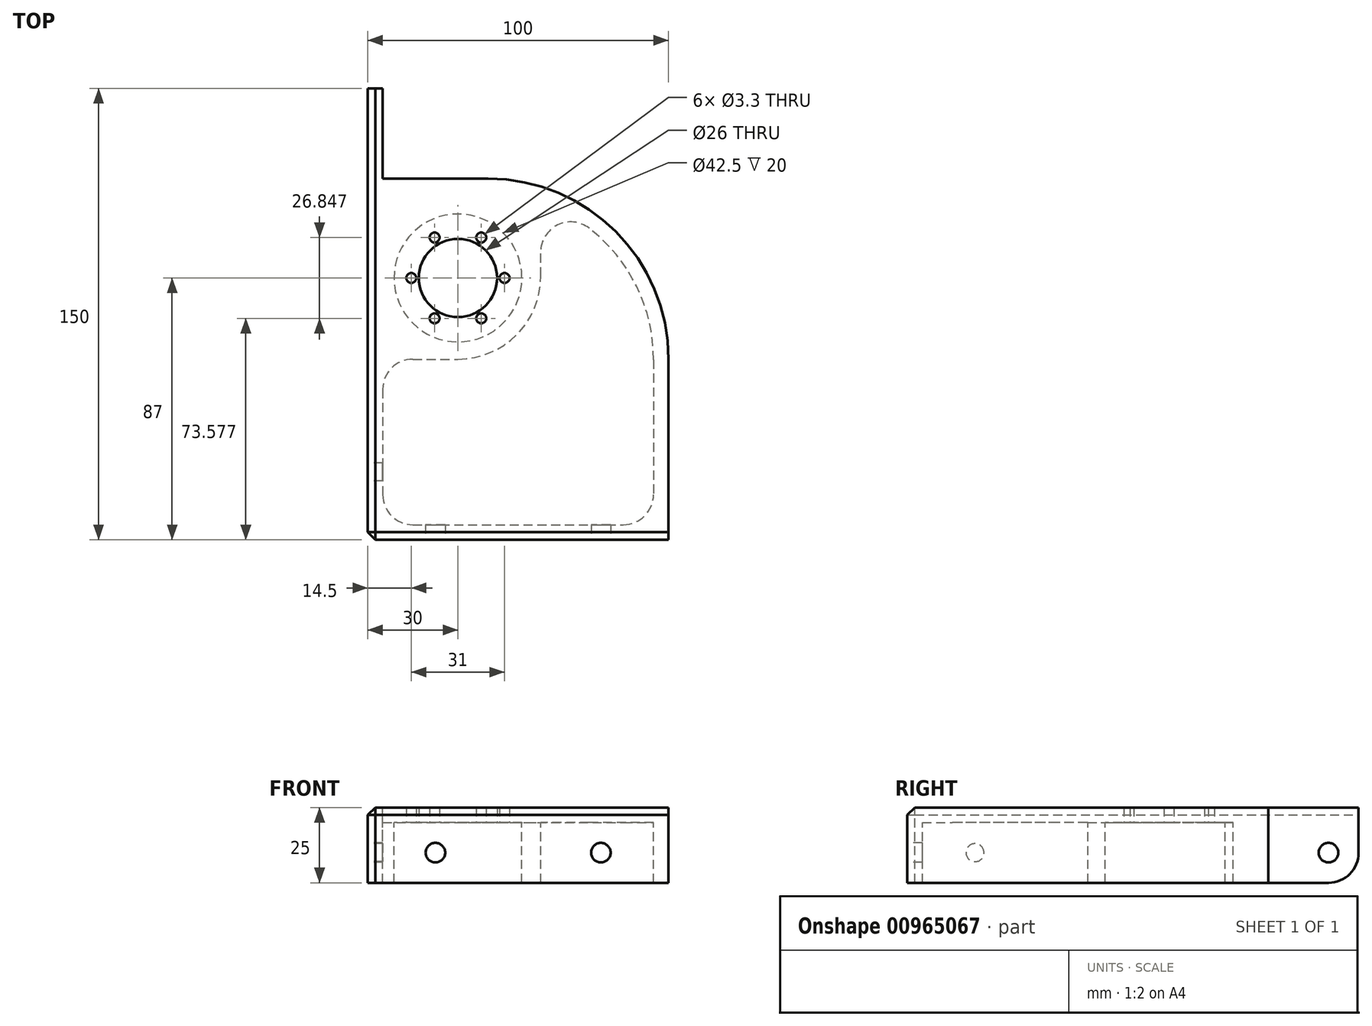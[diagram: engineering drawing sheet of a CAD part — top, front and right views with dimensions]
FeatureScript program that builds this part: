
annotation { "Feature Type Name" : "Feature", "Feature Type Description" : "" }
export const myFeature = defineFeature(function(context is Context, id is Id, definition is map)
    precondition{}
    {
        {
            var Q0;
            Q0=qCreatedBy(makeId("Top.planeOp"),FACE);
            var sketch = newSketch(context, id + "F0", { "sketchPlane" : qUnion([Q0])});
            skLineSegment(sketch, "E0", {"start": v(0, 0) * mm, "end": v(0, 120) * mm});
            skLineSegment(sketch, "E1", {"start": v(100, 0) * mm, "end": v(0, 0) * mm});
            skLineSegment(sketch, "E2", {"start": v(0, 120) * mm, "end": v(5, 120) * mm});
            skLineSegment(sketch, "E3", {"start": v(100, 5) * mm, "end": v(100, 0) * mm});
            skLineSegment(sketch, "E4", {"start": v(5, 120) * mm, "end": v(5, 5) * mm});
            skLineSegment(sketch, "E5", {"start": v(5, 5) * mm, "end": v(100, 5) * mm});
            skCircle(sketch, "E6", {"center": v(30, 87) * mm, "radius": 13 * mm});
            skLineSegment(sketch, "E7", {"start": v(5, 120) * mm, "end": v(40, 120) * mm});
            skLineSegment(sketch, "E8", {"start": v(100, 60) * mm, "end": v(100, 5) * mm});
            skLineSegment(sketch, "E9", {"start": v(44.72, 87) * mm, "end": v(14.37, 87) * mm, "construction": true});
            skLineSegment(sketch, "E10", {"start": v(30, 105.06) * mm, "end": v(30, 59.63) * mm, "construction": true});
            skLineSegment(sketch, "E11", {"start": v(19.21, 97.79) * mm, "end": v(41.7, 75.3) * mm, "construction": true});
            skLineSegment(sketch, "E12", {"start": v(40.55, 97.55) * mm, "end": v(19.07, 76.07) * mm, "construction": true});
            skCircle(sketch, "E13", {"center": v(22.25, 73.58) * mm, "radius": 1.65 * mm});
            skCircle(sketch, "E14.1.0", {"center": v(37.75, 73.58) * mm, "radius": 1.65 * mm});
            skCircle(sketch, "E14.2.0", {"center": v(45.5, 87) * mm, "radius": 1.65 * mm});
            skCircle(sketch, "E14.3.0", {"center": v(37.75, 100.42) * mm, "radius": 1.65 * mm});
            skCircle(sketch, "E14.4.0", {"center": v(22.25, 100.42) * mm, "radius": 1.65 * mm});
            skCircle(sketch, "E14.5.0", {"center": v(14.5, 87) * mm, "radius": 1.65 * mm});
            skPoint(sketch, "E15.visualSharp", {"position": v(100, 120) * mm});
            skArc(sketch, "E15.filletArc", {"start": v(100, 60) * mm, "mid": v(82.43, 102.43) * mm, "end": v(40, 120) * mm});
            skLineSegment(sketch, "E16", {"start": v(-20, -20) * mm, "end": v(-20, 140) * mm, "construction": true});
            skLineSegment(sketch, "E17", {"start": v(-20, 140) * mm, "end": v(0, 140) * mm, "construction": true});
            skLineSegment(sketch, "E18", {"start": v(-10, -167) * mm, "end": v(-10, 160.54) * mm, "construction": true});
            skLineSegment(sketch, "E19", {"start": v(-27.5, -172.08) * mm, "end": v(-27.5, -121.08) * mm, "construction": true});
            skLineSegment(sketch, "E20", {"start": v(-27.5, -121.08) * mm, "end": v(37.5, -121.08) * mm, "construction": true});
            skLineSegment(sketch, "E21", {"start": v(37.5, -121.08) * mm, "end": v(37.5, -127.08) * mm, "construction": true});
            skLineSegment(sketch, "E22", {"start": v(37.5, -127.08) * mm, "end": v(7.5, -127.08) * mm, "construction": true});
            skLineSegment(sketch, "E23", {"start": v(7.5, -127.08) * mm, "end": v(7.5, -172.08) * mm, "construction": true});
            skLineSegment(sketch, "E24", {"start": v(7.5, -172.08) * mm, "end": v(2.5, -172.08) * mm, "construction": true});
            skLineSegment(sketch, "E25", {"start": v(2.5, -172.08) * mm, "end": v(2.5, -127.08) * mm, "construction": true});
            skLineSegment(sketch, "E26", {"start": v(2.5, -127.08) * mm, "end": v(-22.5, -127.08) * mm, "construction": true});
            skLineSegment(sketch, "E27", {"start": v(-22.5, -127.08) * mm, "end": v(-22.5, -172.08) * mm, "construction": true});
            skLineSegment(sketch, "E28", {"start": v(-22.5, -172.08) * mm, "end": v(-27.5, -172.08) * mm, "construction": true});
            skPoint(sketch, "E29", {"position": v(-10, -147.08) * mm});
            skPoint(sketch, "E30", {"position": v(30, -51.08) * mm});
            skLineSegment(sketch, "E31", {"start": v(0, 140) * mm, "end": v(0, 0) * mm, "construction": true});
            skLineSegment(sketch, "E32", {"start": v(140, 0) * mm, "end": v(140, -20) * mm, "construction": true});
            skLineSegment(sketch, "E33", {"start": v(140, 0) * mm, "end": v(0, 0) * mm, "construction": true});
            skLineSegment(sketch, "E34", {"start": v(-20, -20) * mm, "end": v(140, -20) * mm, "construction": true});
            skLineSegment(sketch, "E35", {"start": v(-50.25, -10) * mm, "end": v(191.36, -10) * mm, "construction": true});
            skPoint(sketch, "E36", {"position": v(30, 94) * mm});
            skLineSegment(sketch, "E37", {"start": v(5, 60) * mm, "end": v(30, 60) * mm});
            skLineSegment(sketch, "E38", {"start": v(57.5, 87.5) * mm, "end": v(57.5, 112.14) * mm});
            skArc(sketch, "E39", {"start": v(95, 59.79) * mm, "mid": v(84.71, 92.03) * mm, "end": v(57.5, 112.14) * mm});
            skLineSegment(sketch, "E40", {"start": v(95, 59.79) * mm, "end": v(95, 5) * mm});
            skPoint(sketch, "E41.visualSharp", {"position": v(57.5, 60) * mm});
            skArc(sketch, "E41.filletArc", {"start": v(30, 60) * mm, "mid": v(49.45, 68.05) * mm, "end": v(57.5, 87.5) * mm});
            skCircle(sketch, "E42", {"center": v(30, 87) * mm, "radius": 21.25 * mm});
            skSolve(sketch);
        }
        {
            var Q0;
            Q0=makeQuery(id+"F0.imprint","IMPRINT",FACE,{"disambiguationData":[TD([[makeQuery(id+"F0.imprint","IMPRINT",EDGE,{"derivedFrom":sQuery(id+"F0.wireOp",EDGE,"E0")}),-1.0]])]});
            var Q1;
            Q1=makeQuery(id+"F0.imprint","IMPRINT",FACE,{"disambiguationData":[TD([[makeQuery(id+"F0.imprint","IMPRINT",EDGE,{"derivedFrom":sQuery(id+"F0.wireOp",EDGE,"ppYuwMZk-ploc-tXMn-lUmO-auRrpxJ4f4xt")}),-1.0]])]});
            var Q2;
            Q2=makeQuery(id+"F0.imprint","IMPRINT",FACE,{"disambiguationData":[TD([[makeQuery(id+"F0.imprint","IMPRINT",EDGE,{"derivedFrom":sQuery(id+"F0.wireOp",EDGE,"E4")}),1.0]])]});
            var Q3;
            {var subQ0=sQuery(id+"F0.wireOp",EDGE,"PSJROaDc-Aqwe-zX3O-wr75-Hd8r8wIWMBKI.bottom");Q3=makeQuery(id+"F0.imprint","IMPRINT",FACE,{"disambiguationData":[TD([[makeQuery(id+"F0.imprint","IMPRINT",EDGE,{"derivedFrom":subQ0}),-1.0]])]});}
            var Q4;
            Q4=makeQuery(id+"F0.imprint","IMPRINT",FACE,{"disambiguationData":[TD([[makeQuery(id+"F0.imprint","IMPRINT",EDGE,{"derivedFrom":sQuery(id+"F0.wireOp",EDGE,"NLFgxsRY-dQg0-scZF-8bRf-c5N5ptYbvfvn.top")}),-1.0]])]});
            var Q5;
            {var subQ3=sQuery(id+"F0.wireOp",EDGE,"ZZHPZ1UJ-gQvc-y5dD-WxQZ-NW3lf6L0Z9ZP.top");Q5=makeQuery(id+"F0.imprint","IMPRINT",FACE,{"disambiguationData":[TD([[makeQuery(id+"F0.imprint","IMPRINT",EDGE,{"derivedFrom":subQ3}),1.0]])]});}
            var Q6;
            Q6=makeQuery(id+"F0.imprint","IMPRINT",FACE,{"disambiguationData":[TD([[makeQuery(id+"F0.imprint","IMPRINT",EDGE,{"derivedFrom":sQuery(id+"F0.wireOp",EDGE,"E6")}),-1.0]])]});
            var Q7;
            {var subQ0=sQuery(id+"F0.wireOp",EDGE,"E7");Q7=makeQuery(id+"F0.imprint","IMPRINT",FACE,{"disambiguationData":[TD([[makeQuery(id+"F0.imprint","IMPRINT",EDGE,{"derivedFrom":subQ0}),-1.0]])]});}
            extrude(context, id + "F1", {"entities" : qUnion([Q0, Q1, Q2, Q3, Q4, Q5, Q6, Q7]), "depth" : 5 * mm, "offsetDistance" : 25 * mm});
        }
        {
            var Q0;
            Q0=makeQuery(id+"F0.imprint","IMPRINT",FACE,{"disambiguationData":[TD([[makeQuery(id+"F0.imprint","IMPRINT",EDGE,{"derivedFrom":sQuery(id+"F0.wireOp",EDGE,"E0")}),-1.0]])]});
            var Q1;
            {var subQ0=sQuery(id+"F0.wireOp",EDGE,"PSJROaDc-Aqwe-zX3O-wr75-Hd8r8wIWMBKI.bottom");Q1=makeQuery(id+"F0.imprint","IMPRINT",FACE,{"disambiguationData":[TD([[makeQuery(id+"F0.imprint","IMPRINT",EDGE,{"derivedFrom":subQ0}),-1.0]])]});}
            var Q2;
            Q2=makeQuery(id+"F0.imprint","IMPRINT",FACE,{"disambiguationData":[TD([[makeQuery(id+"F0.imprint","IMPRINT",EDGE,{"derivedFrom":sQuery(id+"F0.wireOp",EDGE,"NLFgxsRY-dQg0-scZF-8bRf-c5N5ptYbvfvn.top")}),-1.0]])]});
            var Q3;
            {var subQ3=sQuery(id+"F0.wireOp",EDGE,"ZZHPZ1UJ-gQvc-y5dD-WxQZ-NW3lf6L0Z9ZP.top");Q3=makeQuery(id+"F0.imprint","IMPRINT",FACE,{"disambiguationData":[TD([[makeQuery(id+"F0.imprint","IMPRINT",EDGE,{"derivedFrom":subQ3}),1.0]])]});}
            var Q4;
            {var subQ0=sQuery(id+"F0.wireOp",EDGE,"E7");Q4=makeQuery(id+"F0.imprint","IMPRINT",FACE,{"disambiguationData":[TD([[makeQuery(id+"F0.imprint","IMPRINT",EDGE,{"derivedFrom":subQ0}),-1.0]])]});}
            extrude(context, id + "F2", {"entities" : qUnion([Q0, Q1, Q2, Q3, Q4]), "operationType" : NewBodyOperationType.ADD, "oppositeDirection" : true, "depth" : 20 * mm, "offsetDistance" : 25 * mm});
        }
        {
            var Q0;
            {var subQ0=sQuery(id+"F0.wireOp",EDGE,"E7");var subQ1=sQuery(id+"F0.wireOp",EDGE,"E2");Q0=makeQuery(id+"F2.boolean.opBoolean","MERGE",FACE,{"derivedFrom":[makeQuery(id+"F1.opExtrude","SWEPT_FACE",FACE,{"disambiguationData":[OSD([subQ1,subQ0])]}),makeQuery(id+"F2.opExtrude","SWEPT_FACE",FACE,{"disambiguationData":[OSD([subQ1,subQ0])]})]});}
            var sketch = newSketch(context, id + "F3", { "sketchPlane" : qUnion([Q0])});
            skLineSegment(sketch, "E43.bottom", {"start": v(0, -20) * mm, "end": v(-5, -20) * mm});
            skLineSegment(sketch, "E43.top", {"start": v(0, 5) * mm, "end": v(-5, 5) * mm});
            skLineSegment(sketch, "E43.left", {"start": v(0, -20) * mm, "end": v(0, 5) * mm});
            skLineSegment(sketch, "E43.right", {"start": v(-5, -20) * mm, "end": v(-5, 5) * mm});
            skSolve(sketch);
        }
        {
            var Q0;
            {var subQ1=sQuery(id+"F3.wireOp",EDGE,"E43.bottom");Q0=makeQuery(id+"F3.imprint","IMPRINT",FACE,{"disambiguationData":[TD([[makeQuery(id+"F3.imprint","IMPRINT",EDGE,{"derivedFrom":subQ1}),-1.0]])]});}
            extrude(context, id + "F4", {"entities" : qUnion([Q0]), "operationType" : NewBodyOperationType.ADD, "depth" : 30 * mm, "offsetDistance" : 25 * mm});
        }
        {
            var Q0;
            {var subQ0=sQuery(id+"F0.wireOp",EDGE,"E0");Q0=makeQuery(id+"F2.boolean.opBoolean","MERGE",FACE,{"derivedFrom":[makeQuery(id+"F1.opExtrude","SWEPT_FACE",FACE,{"disambiguationData":[OSD([subQ0])]}),makeQuery(id+"F2.opExtrude","SWEPT_FACE",FACE,{"disambiguationData":[OSD([subQ0])]})]});}
            var sketch = newSketch(context, id + "F5", { "sketchPlane" : qUnion([Q0])});
            skCircle(sketch, "E44", {"center": v(-140, -10) * mm, "radius": 3.25 * mm});
            skCircle(sketch, "E45", {"center": v(-22.5, -10) * mm, "radius": 3 * mm});
            skSolve(sketch);
        }
        {
            var Q0;
            {var subQ0=sQuery(id+"F0.wireOp",EDGE,"E1");Q0=makeQuery(id+"F2.boolean.opBoolean","MERGE",FACE,{"derivedFrom":[makeQuery(id+"F1.opExtrude","SWEPT_FACE",FACE,{"disambiguationData":[OSD([subQ0])]}),makeQuery(id+"F2.opExtrude","SWEPT_FACE",FACE,{"disambiguationData":[OSD([subQ0])]})]});}
            var sketch = newSketch(context, id + "F6", { "sketchPlane" : qUnion([Q0])});
            skCircle(sketch, "E46", {"center": v(22.5, -10) * mm, "radius": 3.25 * mm});
            skCircle(sketch, "E47", {"center": v(77.5, -10) * mm, "radius": 3.25 * mm});
            skSolve(sketch);
        }
        {
            var Q0;
            Q0=makeQuery(id+"F6.imprint","IMPRINT",FACE,{"disambiguationData":[TD([[makeQuery(id+"F6.imprint","IMPRINT",EDGE,{"derivedFrom":sQuery(id+"F6.wireOp",EDGE,"E46")}),1.0]])]});
            var Q1;
            Q1=makeQuery(id+"F6.imprint","IMPRINT",FACE,{"disambiguationData":[TD([[makeQuery(id+"F6.imprint","IMPRINT",EDGE,{"derivedFrom":sQuery(id+"F6.wireOp",EDGE,"E47")}),1.0]])]});
            extrude(context, id + "F7", {"entities" : qUnion([Q0, Q1]), "operationType" : NewBodyOperationType.REMOVE, "oppositeDirection" : true, "depth" : 25 * mm, "offsetDistance" : 25 * mm});
        }
        {
            var Q0;
            Q0=makeQuery(id+"F5.imprint","IMPRINT",FACE,{"disambiguationData":[TD([[makeQuery(id+"F5.imprint","IMPRINT",EDGE,{"derivedFrom":sQuery(id+"F5.wireOp",EDGE,"E45")}),1.0]])]});
            var Q1;
            Q1=makeQuery(id+"F5.imprint","IMPRINT",FACE,{"disambiguationData":[TD([[makeQuery(id+"F5.imprint","IMPRINT",EDGE,{"derivedFrom":sQuery(id+"F5.wireOp",EDGE,"E44")}),1.0]])]});
            extrude(context, id + "F8", {"entities" : qUnion([Q0, Q1]), "operationType" : NewBodyOperationType.REMOVE, "oppositeDirection" : true, "depth" : 25 * mm, "offsetDistance" : 25 * mm});
        }
        {
            var Q0;
            Q0=makeQuery(id+"F1.opExtrude","CAP_EDGE",EDGE,{"disambiguationData":[OSD([sQuery(id+"F0.wireOp",EDGE,"E1")])],"isStart":false});
            var Q1;
            Q1=makeQuery(id+"F1.opExtrude","CAP_EDGE",EDGE,{"disambiguationData":[OSD([sQuery(id+"F0.wireOp",EDGE,"E0")])],"isStart":false});
            var Q2;
            {var subQ0=sQuery(id+"F0.wireOp",EDGE,"E1");var subQ1=sQuery(id+"F0.wireOp",EDGE,"E0");Q2=makeQuery(id+"F2.boolean.opBoolean","MERGE",EDGE,{"derivedFrom":[makeQuery(id+"F1.opExtrude","SWEPT_EDGE",EDGE,{"disambiguationData":[OSD([subQ1,subQ0])]}),makeQuery(id+"F2.opExtrude","SWEPT_EDGE",EDGE,{"disambiguationData":[OSD([subQ1,subQ0])]})]});}
            chamfer(context, id + "F9", {"entities" : qUnion([Q0, Q1, Q2]), "width" : 2.5 * mm, "tangentPropagation" : true});
        }
        {
            var Q0;
            Q0=makeQuery(id+"F2.opExtrude","SWEPT_EDGE",EDGE,{"disambiguationData":[OSD([sQuery(id+"F0.wireOp",EDGE,"E4"),sQuery(id+"F0.wireOp",EDGE,"E5")])]});
            var Q1;
            Q1=makeQuery(id+"F2.opExtrude","SWEPT_EDGE",EDGE,{"disambiguationData":[OSD([sQuery(id+"F0.wireOp",EDGE,"E4"),sQuery(id+"F0.wireOp",EDGE,"E37")])]});
            var Q2;
            Q2=makeQuery(id+"F2.opExtrude","SWEPT_EDGE",EDGE,{"disambiguationData":[OSD([sQuery(id+"F0.wireOp",EDGE,"E38"),sQuery(id+"F0.wireOp",EDGE,"E39")])]});
            var Q3;
            Q3=makeQuery(id+"F2.opExtrude","SWEPT_EDGE",EDGE,{"disambiguationData":[OSD([sQuery(id+"F0.wireOp",EDGE,"E5"),sQuery(id+"F0.wireOp",EDGE,"E40")])]});
            var Q4;
            Q4=makeQuery(id+"F4.opExtrude","CAP_EDGE",EDGE,{"disambiguationData":[OSD([sQuery(id+"F3.wireOp",EDGE,"E43.right")])],"isStart":true});
            var Q5;
            Q5=makeQuery(id+"F4.opExtrude","CAP_EDGE",EDGE,{"disambiguationData":[OSD([sQuery(id+"F3.wireOp",EDGE,"E43.bottom")])],"isStart":false});
            fillet(context, id + "F10", {"entities" : qUnion([Q0, Q1, Q2, Q3, Q4, Q5]), "tangentPropagation" : true, "radius" : 10 * mm, "defaultsChanged" : false, "vertexSettings" : [], "allowEdgeOverflow" : false});
        }
    });
